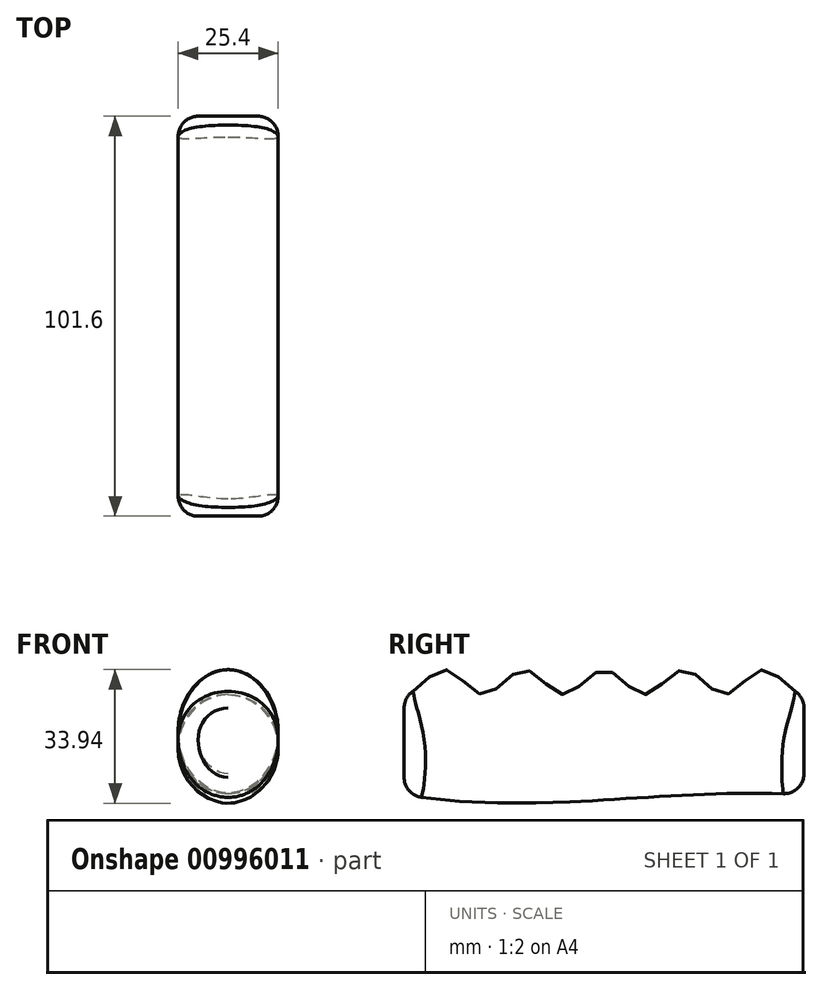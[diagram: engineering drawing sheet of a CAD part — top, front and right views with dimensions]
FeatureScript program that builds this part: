
annotation { "Feature Type Name" : "Feature", "Feature Type Description" : "" }
export const myFeature = defineFeature(function(context is Context, id is Id, definition is map)
    precondition{}
    {
        {
            var Q0;
            Q0=qCreatedBy(makeId("Front.planeOp"),FACE);
            var sketch = newSketch(context, id + "F0", { "sketchPlane" : qUnion([Q0])});
            skCircle(sketch, "E0", {"center": v(0, 0) * mm, "radius": 12.7 * mm});
            skSolve(sketch);
        }
        {
            var Q0;
            Q0=qCreatedBy(makeId("Front.planeOp"),FACE);
            cPlane(context, id + "F1", {"entities" : qUnion([Q0]), "cplaneType" : CPlaneType.OFFSET, "offset" : 101.6 * mm, "width" : 152.4 * mm, "height" : 152.4 * mm});
        }
        {
            var Q0;
            Q0=qCreatedBy(id+"F1.planeOp",FACE);
            var sketch = newSketch(context, id + "F2", { "sketchPlane" : qUnion([Q0])});
            skCircle(sketch, "E1", {"center": v(0, 0) * mm, "radius": 12.7 * mm});
            skSolve(sketch);
        }
        {
            var Q0;
            Q0=qCreatedBy(makeId("Right.planeOp"),FACE);
            var sketch = newSketch(context, id + "F3", { "sketchPlane" : qUnion([Q0])});
            skLineSegment(sketch, "E2.0", {"start": v(0, -12.7) * mm, "end": v(0, 12.7) * mm, "construction": true});
            skLineSegment(sketch, "E3.0", {"start": v(-101.6, -12.7) * mm, "end": v(-101.6, 12.7) * mm, "construction": true});
            skFitSpline(sketch, "E4", {"points": [v(0, 12.7) * mm, v(-10.16, 19.05) * mm, v(-20.32, 12.7) * mm, v(-30.48, 19.05) * mm, v(-40.64, 12.7) * mm, v(-50.8, 19.05) * mm, v(-60.96, 12.7) * mm, v(-71.12, 19.05) * mm, v(-81.28, 12.7) * mm, v(-91.44, 19.05) * mm, v(-101.6, 12.7) * mm], "startDerivative": vector(-95.25, 0) * mm, "endDerivative": vector(-95.25, 0) * mm});
            skLineSegment(sketch, "E5", {"start": v(-10.16, 19.05) * mm, "end": v(-30.48, 19.05) * mm, "construction": true});
            skLineSegment(sketch, "E6", {"start": v(-30.48, 19.05) * mm, "end": v(-50.8, 19.05) * mm, "construction": true});
            skLineSegment(sketch, "E7", {"start": v(-50.8, 19.05) * mm, "end": v(-71.12, 19.05) * mm, "construction": true});
            skLineSegment(sketch, "E8", {"start": v(-71.12, 19.05) * mm, "end": v(-91.44, 19.05) * mm, "construction": true});
            skLineSegment(sketch, "E9", {"start": v(0, 12.7) * mm, "end": v(-20.32, 12.7) * mm, "construction": true});
            skLineSegment(sketch, "E10", {"start": v(-20.32, 12.7) * mm, "end": v(-40.64, 12.7) * mm, "construction": true});
            skLineSegment(sketch, "E11", {"start": v(-40.64, 12.7) * mm, "end": v(-60.96, 12.7) * mm, "construction": true});
            skLineSegment(sketch, "E12", {"start": v(-60.96, 12.7) * mm, "end": v(-81.28, 12.7) * mm, "construction": true});
            skLineSegment(sketch, "E13", {"start": v(-81.28, 12.7) * mm, "end": v(-101.6, 12.7) * mm, "construction": true});
            skLineSegment(sketch, "E14", {"start": v(-10.16, 19.05) * mm, "end": v(0, 19.05) * mm, "construction": true});
            skLineSegment(sketch, "E15", {"start": v(-91.44, 19.05) * mm, "end": v(-101.6, 19.05) * mm, "construction": true});
            skLineSegment(sketch, "E16", {"start": v(-40.64, 12.7) * mm, "end": v(-40.64, 19.05) * mm, "construction": true});
            skSolve(sketch);
        }
        {
            var Q0;
            Q0=qCreatedBy(makeId("Right.planeOp"),FACE);
            var sketch = newSketch(context, id + "F4", { "sketchPlane" : qUnion([Q0])});
            skFitSpline(sketch, "E17", {"points": [v(0, -12.7) * mm, v(-101.6, -12.7) * mm], "startDerivative": vector(-107.22, 6.24) * mm, "endDerivative": vector(-101.6, 17.49) * mm});
            skSolve(sketch);
        }
        {
            var Q0;
            Q0=makeQuery(id+"F0.imprint","IMPRINT",FACE,{"disambiguationData":[TD([[makeQuery(id+"F0.imprint","IMPRINT",EDGE,{"derivedFrom":sQuery(id+"F0.wireOp",EDGE,"E0")}),1.0]])]});
            var Q1;
            Q1=makeQuery(id+"F2.imprint","IMPRINT",FACE,{"disambiguationData":[TD([[makeQuery(id+"F2.imprint","IMPRINT",EDGE,{"derivedFrom":sQuery(id+"F2.wireOp",EDGE,"E1")}),1.0]])]});
            var Q2;
            Q2=sQuery(id+"F3.wireOp",EDGE,"E4");
            var Q3;
            Q3=sQuery(id+"FUk3hhU1X4bUE3Y_0.1.F4.wireOp",EDGE,"E17");
            var Q4;
            Q4=sQuery(id+"FUk3hhU1X4bUE3Y_0.3.F4.wireOp",EDGE,"E17");
            var Q5;
            Q5=sQuery(id+"F4.wireOp",EDGE,"E17");
            loft(context, id + "F5", {"addGuides" : true, "sheetProfilesArray" : [{ "sheetProfileEntities" : qUnion([Q0]) }, { "sheetProfileEntities" : qUnion([Q1]) }], "guidesArray" : [{ "guideEntities" : qUnion([Q2]), "guideDerivativeType" : LoftGuideDerivativeType.DEFAULT, "guideDerivativeMagnitude" : 1 }, { "guideEntities" : qUnion([Q3]), "guideDerivativeType" : LoftGuideDerivativeType.DEFAULT, "guideDerivativeMagnitude" : 1 }, { "guideEntities" : qUnion([Q4]), "guideDerivativeType" : LoftGuideDerivativeType.DEFAULT, "guideDerivativeMagnitude" : 1 }, { "guideEntities" : qUnion([Q5]), "guideDerivativeType" : LoftGuideDerivativeType.DEFAULT, "guideDerivativeMagnitude" : 1 }]});
        }
        {
            var Q0;
            Q0=makeQuery(id+"F5.opLoft","MID_CAP_EDGE",EDGE,{"disambiguationData":[OSD([sQuery(id+"F0.wireOp",EDGE,"E0"),sQuery(id+"F3.wireOp",EDGE,"E4"),sQuery(id+"FUk3hhU1X4bUE3Y_0.3.F4.wireOp",EDGE,"E17")])],"capPos":0.0});
            var Q1;
            Q1=makeQuery(id+"F5.opLoft","MID_CAP_EDGE",EDGE,{"disambiguationData":[OSD([sQuery(id+"F2.wireOp",EDGE,"E1"),sQuery(id+"F3.wireOp",EDGE,"E4"),sQuery(id+"FUk3hhU1X4bUE3Y_0.3.F4.wireOp",EDGE,"E17")])],"capPos":1.0});
            fillet(context, id + "F6", {"entities" : qUnion([Q0, Q1]), "radius" : 5.08 * mm, "tangentPropagation" : true, "allowEdgeOverflow" : false});
        }
    });
